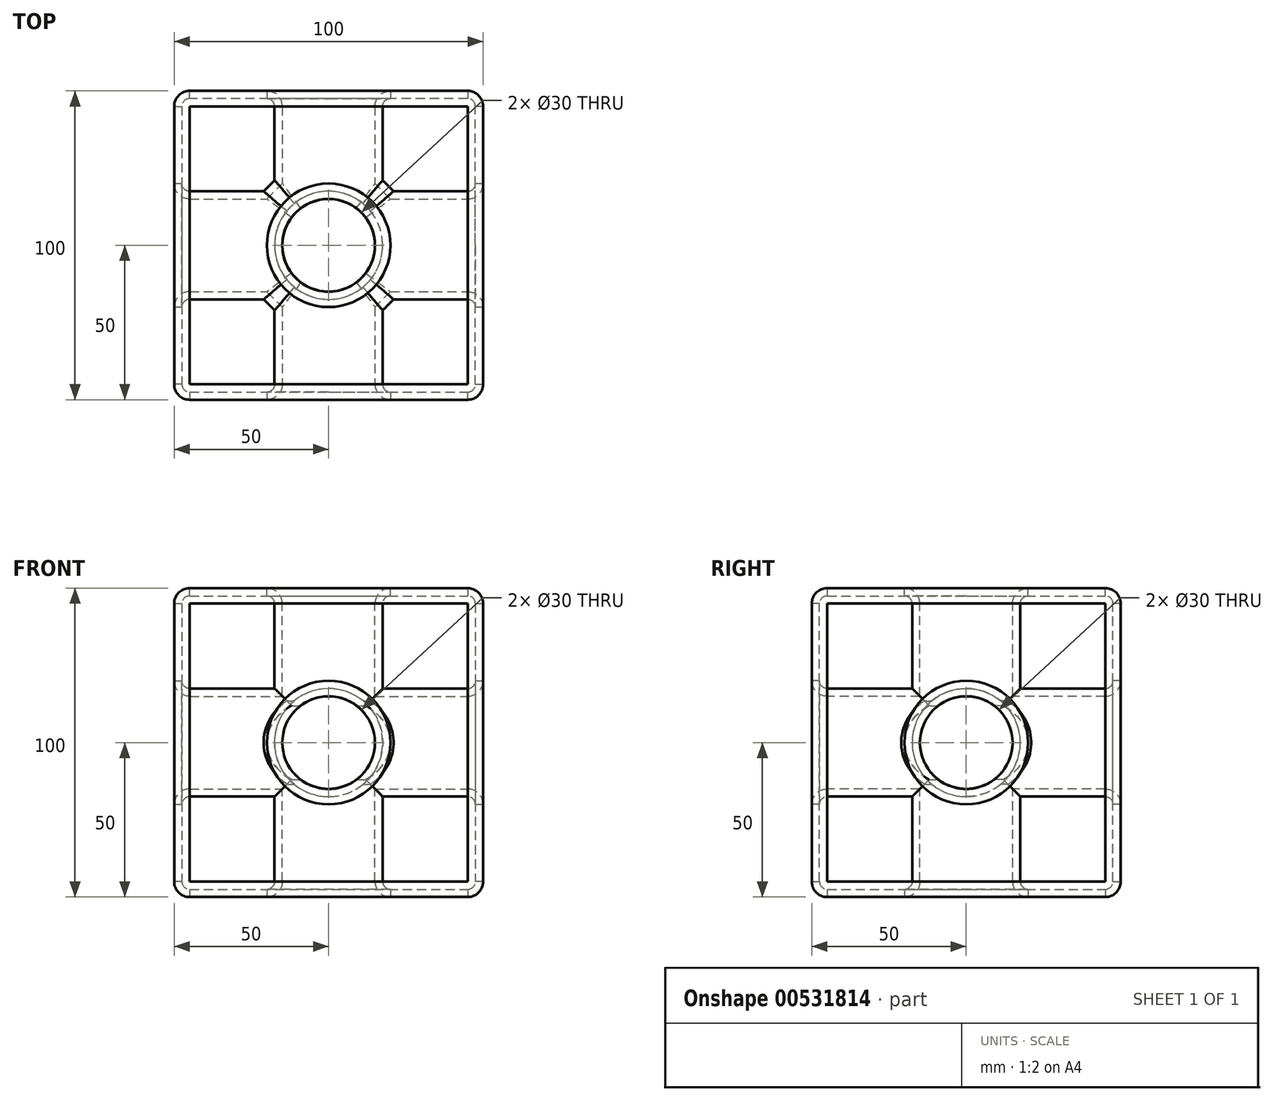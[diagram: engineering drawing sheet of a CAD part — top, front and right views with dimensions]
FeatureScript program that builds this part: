
annotation { "Feature Type Name" : "Feature", "Feature Type Description" : "" }
export const myFeature = defineFeature(function(context is Context, id is Id, definition is map)
    precondition{}
    {
        {
            var Q0;
            Q0=qCreatedBy(makeId("Front.planeOp"),FACE);
            var sketch = newSketch(context, id + "F0", { "sketchPlane" : qUnion([Q0])});
            skLineSegment(sketch, "E0.bottom", {"start": v(-50, 50) * mm, "end": v(50, 50) * mm});
            skLineSegment(sketch, "E0.top", {"start": v(-50, -50) * mm, "end": v(50, -50) * mm});
            skLineSegment(sketch, "E0.left", {"start": v(-50, 50) * mm, "end": v(-50, -50) * mm});
            skLineSegment(sketch, "E0.right", {"start": v(50, 50) * mm, "end": v(50, -50) * mm});
            skPoint(sketch, "E0.middle", {"position": v(0, 0) * mm});
            skSolve(sketch);
        }
        {
            var Q0;
            Q0=makeQuery(id+"F0.imprint","IMPRINT",FACE,{"disambiguationData":[TD([[makeQuery(id+"F0.imprint","IMPRINT",EDGE,{"derivedFrom":sQuery(id+"F0.wireOp",EDGE,"E0.bottom")}),-1.0]])]});
            extrude(context, id + "F1", {"entities" : qUnion([Q0]), "endBound" : BoundingType.SYMMETRIC, "depth" : 100 * mm, "offsetDistance" : 25 * mm});
        }
        {
            var Q0;
            Q0=makeQuery(id+"F1.opExtrude","SWEPT_FACE",FACE,{"disambiguationData":[OSD([sQuery(id+"F0.wireOp",EDGE,"E0.bottom")])]});
            var sketch = newSketch(context, id + "F2", { "sketchPlane" : qUnion([Q0])});
            skCircle(sketch, "E1", {"center": v(0, 0) * mm, "radius": 15 * mm});
            skSolve(sketch);
        }
        {
            var Q0;
            Q0 = qSketchRegion(id + "F2", true);
            extrude(context, id + "F3", {"entities" : qUnion([Q0]), "operationType" : NewBodyOperationType.REMOVE, "oppositeDirection" : true, "depth" : 110 * mm, "offsetDistance" : 25 * mm});
        }
        {
            var Q0;
            Q0=makeQuery(id+"F1.opExtrude","CAP_FACE",FACE,{"disambiguationData":[OSD([sQuery(id+"F0.wireOp",EDGE,"E0.bottom"),sQuery(id+"F0.wireOp",EDGE,"E0.top"),sQuery(id+"F0.wireOp",EDGE,"E0.left"),sQuery(id+"F0.wireOp",EDGE,"E0.right")])],"isStart":false});
            var sketch = newSketch(context, id + "F4", { "sketchPlane" : qUnion([Q0])});
            skCircle(sketch, "E2", {"center": v(0, 0) * mm, "radius": 15 * mm});
            skSolve(sketch);
        }
        {
            var Q0;
            Q0 = qSketchRegion(id + "F4", true);
            extrude(context, id + "F5", {"entities" : qUnion([Q0]), "operationType" : NewBodyOperationType.REMOVE, "oppositeDirection" : true, "depth" : 110 * mm, "offsetDistance" : 25 * mm});
        }
        {
            var Q0;
            Q0=makeQuery(id+"F1.opExtrude","SWEPT_FACE",FACE,{"disambiguationData":[OSD([sQuery(id+"F0.wireOp",EDGE,"E0.right")])]});
            var sketch = newSketch(context, id + "F6", { "sketchPlane" : qUnion([Q0])});
            skCircle(sketch, "E3", {"center": v(0, 0) * mm, "radius": 15 * mm});
            skSolve(sketch);
        }
        {
            var Q0;
            Q0 = qSketchRegion(id + "F6", true);
            extrude(context, id + "F7", {"entities" : qUnion([Q0]), "operationType" : NewBodyOperationType.REMOVE, "oppositeDirection" : true, "depth" : 100 * mm, "offsetDistance" : 25 * mm});
        }
        {
            var Q0;
            {var subQ0=makeQuery(id+"F5.opExtrude","SWEPT_FACE",FACE,{"disambiguationData":[OSD([sQuery(id+"F4.wireOp",EDGE,"E2")])]});Q0=makeQuery(id+"F7.boolean.opBoolean","INTERSECT",EDGE,{"disambiguationData":[OD(1.0)],"derivedFrom":[makeQuery(id+"F5.boolean.opBoolean","COPY",FACE,{"disambiguationData":[TD([makeQuery(id+"F1.opExtrude","CAP_FACE",FACE,{"disambiguationData":[OSD([sQuery(id+"F0.wireOp",EDGE,"E0.bottom"),sQuery(id+"F0.wireOp",EDGE,"E0.top"),sQuery(id+"F0.wireOp",EDGE,"E0.left"),sQuery(id+"F0.wireOp",EDGE,"E0.right")])],"isStart":false})])],"derivedFrom":subQ0}),makeQuery(id+"F7.opExtrude","SWEPT_FACE",FACE,{"disambiguationData":[OSD([sQuery(id+"F6.wireOp",EDGE,"E3")])]})]});}
            var Q1;
            {var subQ0=makeQuery(id+"F5.opExtrude","SWEPT_FACE",FACE,{"disambiguationData":[OSD([sQuery(id+"F4.wireOp",EDGE,"E2")])]});Q1=makeQuery(id+"F7.boolean.opBoolean","INTERSECT",EDGE,{"disambiguationData":[OD(0.0)],"derivedFrom":[makeQuery(id+"F5.boolean.opBoolean","COPY",FACE,{"disambiguationData":[TD([makeQuery(id+"F1.opExtrude","CAP_FACE",FACE,{"disambiguationData":[OSD([sQuery(id+"F0.wireOp",EDGE,"E0.bottom"),sQuery(id+"F0.wireOp",EDGE,"E0.top"),sQuery(id+"F0.wireOp",EDGE,"E0.left"),sQuery(id+"F0.wireOp",EDGE,"E0.right")])],"isStart":true})])],"derivedFrom":subQ0}),makeQuery(id+"F7.opExtrude","SWEPT_FACE",FACE,{"disambiguationData":[OSD([sQuery(id+"F6.wireOp",EDGE,"E3")])]})]});}
            var Q2;
            {var subQ0=makeQuery(id+"F5.opExtrude","SWEPT_FACE",FACE,{"disambiguationData":[OSD([sQuery(id+"F4.wireOp",EDGE,"E2")])]});Q2=makeQuery(id+"F7.boolean.opBoolean","INTERSECT",EDGE,{"disambiguationData":[OD(1.0)],"derivedFrom":[makeQuery(id+"F5.boolean.opBoolean","COPY",FACE,{"disambiguationData":[TD([makeQuery(id+"F1.opExtrude","CAP_FACE",FACE,{"disambiguationData":[OSD([sQuery(id+"F0.wireOp",EDGE,"E0.bottom"),sQuery(id+"F0.wireOp",EDGE,"E0.top"),sQuery(id+"F0.wireOp",EDGE,"E0.left"),sQuery(id+"F0.wireOp",EDGE,"E0.right")])],"isStart":true})])],"derivedFrom":subQ0}),makeQuery(id+"F7.opExtrude","SWEPT_FACE",FACE,{"disambiguationData":[OSD([sQuery(id+"F6.wireOp",EDGE,"E3")])]})]});}
            var Q3;
            {var subQ0=makeQuery(id+"F5.opExtrude","SWEPT_FACE",FACE,{"disambiguationData":[OSD([sQuery(id+"F4.wireOp",EDGE,"E2")])]});Q3=makeQuery(id+"F7.boolean.opBoolean","INTERSECT",EDGE,{"disambiguationData":[OD(0.0)],"derivedFrom":[makeQuery(id+"F5.boolean.opBoolean","COPY",FACE,{"disambiguationData":[TD([makeQuery(id+"F1.opExtrude","CAP_FACE",FACE,{"disambiguationData":[OSD([sQuery(id+"F0.wireOp",EDGE,"E0.bottom"),sQuery(id+"F0.wireOp",EDGE,"E0.top"),sQuery(id+"F0.wireOp",EDGE,"E0.left"),sQuery(id+"F0.wireOp",EDGE,"E0.right")])],"isStart":false})])],"derivedFrom":subQ0}),makeQuery(id+"F7.opExtrude","SWEPT_FACE",FACE,{"disambiguationData":[OSD([sQuery(id+"F6.wireOp",EDGE,"E3")])]})]});}
            chamfer(context, id + "F8", {"entities" : qUnion([Q0, Q1, Q2, Q3]), "width" : 5 * mm, "tangentPropagation" : true});
        }
        {
            var Q0;
            Q0=makeQuery(id+"F1.opExtrude","CAP_EDGE",EDGE,{"disambiguationData":[OSD([sQuery(id+"F0.wireOp",EDGE,"E0.left")])],"isStart":true});
            var Q1;
            Q1=makeQuery(id+"F1.opExtrude","SWEPT_FACE",FACE,{"disambiguationData":[OSD([sQuery(id+"F0.wireOp",EDGE,"E0.left")])]});
            var Q2;
            Q2=makeQuery(id+"F1.opExtrude","CAP_FACE",FACE,{"disambiguationData":[OSD([sQuery(id+"F0.wireOp",EDGE,"E0.bottom"),sQuery(id+"F0.wireOp",EDGE,"E0.top"),sQuery(id+"F0.wireOp",EDGE,"E0.left"),sQuery(id+"F0.wireOp",EDGE,"E0.right")])],"isStart":false});
            var Q3;
            Q3=makeQuery(id+"F1.opExtrude","SWEPT_FACE",FACE,{"disambiguationData":[OSD([sQuery(id+"F0.wireOp",EDGE,"E0.right")])]});
            var Q4;
            Q4=makeQuery(id+"F1.opExtrude","CAP_FACE",FACE,{"disambiguationData":[OSD([sQuery(id+"F0.wireOp",EDGE,"E0.bottom"),sQuery(id+"F0.wireOp",EDGE,"E0.top"),sQuery(id+"F0.wireOp",EDGE,"E0.left"),sQuery(id+"F0.wireOp",EDGE,"E0.right")])],"isStart":true});
            var Q5;
            Q5=makeQuery(id+"F1.opExtrude","SWEPT_FACE",FACE,{"disambiguationData":[OSD([sQuery(id+"F0.wireOp",EDGE,"E0.top")])]});
            var Q6;
            Q6=makeQuery(id+"F1.opExtrude","SWEPT_FACE",FACE,{"disambiguationData":[OSD([sQuery(id+"F0.wireOp",EDGE,"E0.bottom")])]});
            fillet(context, id + "F9", {"entities" : qUnion([Q0, Q1, Q2, Q3, Q4, Q5, Q6]), "radius" : 5 * mm, "tangentPropagation" : true, "allowEdgeOverflow" : false});
        }
        {
            var Q0;
            Q0=makeQuery(id+"F1.opExtrude","CAP_FACE",FACE,{"disambiguationData":[OSD([sQuery(id+"F0.wireOp",EDGE,"E0.bottom"),sQuery(id+"F0.wireOp",EDGE,"E0.top"),sQuery(id+"F0.wireOp",EDGE,"E0.left"),sQuery(id+"F0.wireOp",EDGE,"E0.right")])],"isStart":false});
            var Q1;
            Q1=makeQuery(id+"F1.opExtrude","SWEPT_FACE",FACE,{"disambiguationData":[OSD([sQuery(id+"F0.wireOp",EDGE,"E0.left")])]});
            var Q2;
            Q2=makeQuery(id+"F1.opExtrude","SWEPT_FACE",FACE,{"disambiguationData":[OSD([sQuery(id+"F0.wireOp",EDGE,"E0.right")])]});
            var Q3;
            Q3=makeQuery(id+"F1.opExtrude","CAP_FACE",FACE,{"disambiguationData":[OSD([sQuery(id+"F0.wireOp",EDGE,"E0.bottom"),sQuery(id+"F0.wireOp",EDGE,"E0.top"),sQuery(id+"F0.wireOp",EDGE,"E0.left"),sQuery(id+"F0.wireOp",EDGE,"E0.right")])],"isStart":true});
            var Q4;
            Q4=makeQuery(id+"F1.opExtrude","SWEPT_FACE",FACE,{"disambiguationData":[OSD([sQuery(id+"F0.wireOp",EDGE,"E0.bottom")])]});
            shell(context, id + "F10", {"entities" : qUnion([Q0, Q1, Q2, Q3, Q4]), "thickness" : 2.5 * mm});
        }
        {
            var Q0;
            Q0=makeQuery(id+"F1.opExtrude","SWEPT_FACE",FACE,{"disambiguationData":[OSD([sQuery(id+"F0.wireOp",EDGE,"E0.top")])]});
            extrude(context, id + "F11", {"entities" : qUnion([Q0]), "operationType" : NewBodyOperationType.REMOVE, "oppositeDirection" : true, "depth" : 25 * mm, "offsetDistance" : 25 * mm});
        }
    });
